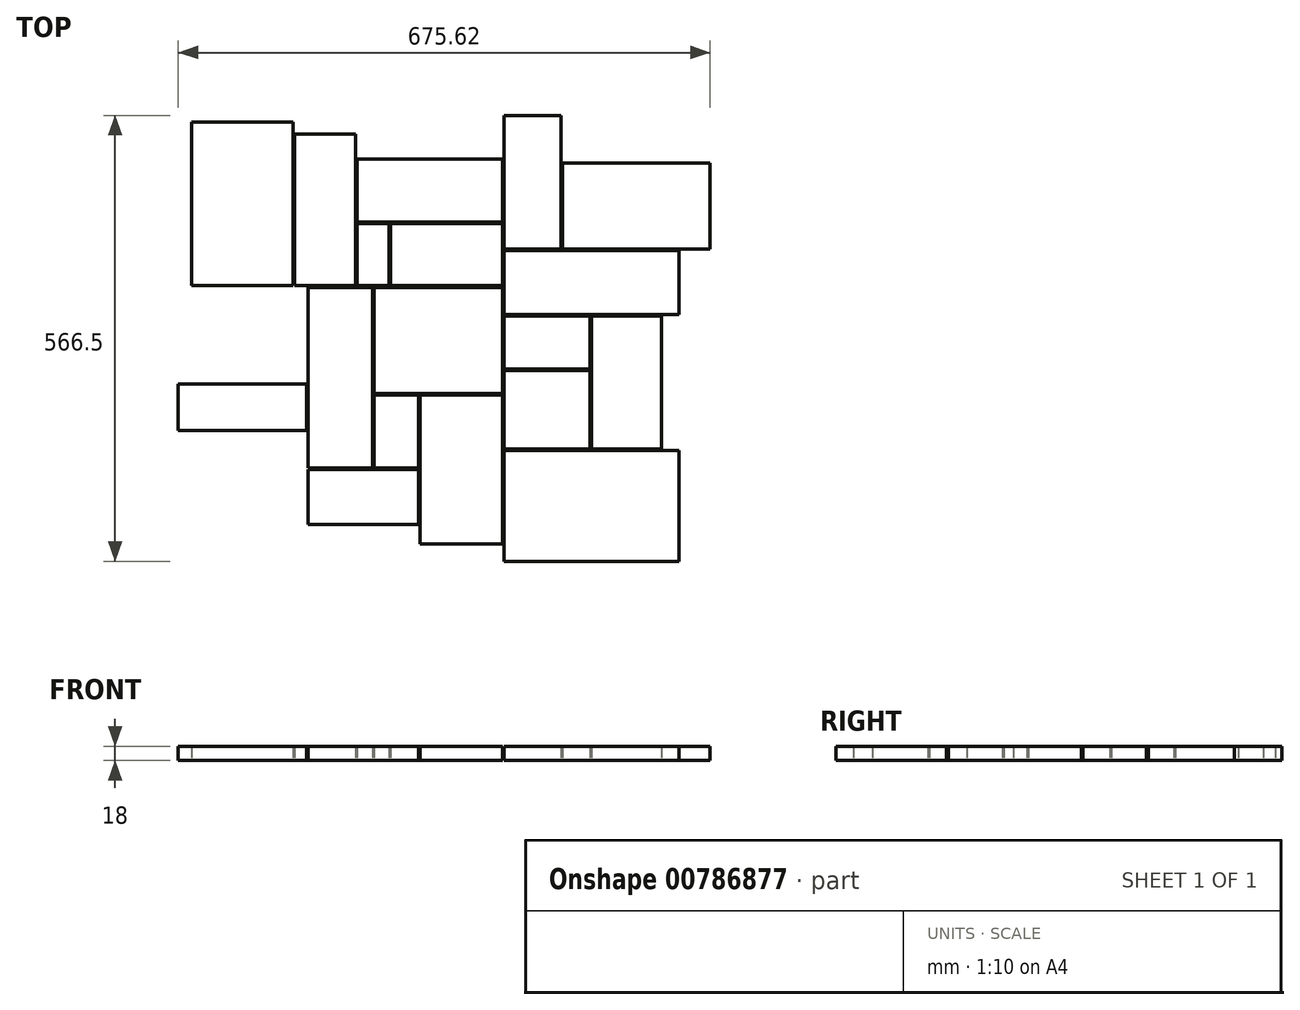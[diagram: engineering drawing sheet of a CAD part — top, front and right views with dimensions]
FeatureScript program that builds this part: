
annotation { "Feature Type Name" : "Feature", "Feature Type Description" : "" }
export const myFeature = defineFeature(function(context is Context, id is Id, definition is map)
    precondition{}
    {
        {
            var Q0;
            Q0=qCreatedBy(makeId("Top.planeOp"),FACE);
            var sketch = newSketch(context, id + "F0", { "sketchPlane" : qUnion([Q0])});
            skLineSegment(sketch, "E0.top", {"start": v(-7.38, -279.05) * mm, "end": v(214.62, -279.05) * mm});
            skLineSegment(sketch, "E0.right", {"start": v(214.62, -138.55) * mm, "end": v(214.62, -279.05) * mm});
            skLineSegment(sketch, "E1.right", {"start": v(192.62, -136.55) * mm, "end": v(192.62, 32.45) * mm});
            skLineSegment(sketch, "E2.right", {"start": v(214.62, 34.45) * mm, "end": v(214.62, 115.45) * mm});
            skLineSegment(sketch, "E3.top", {"start": v(-7.38, 287.45) * mm, "end": v(64.62, 287.45) * mm});
            skLineSegment(sketch, "E4.top", {"start": v(66.62, 226.95) * mm, "end": v(254.12, 226.95) * mm});
            skLineSegment(sketch, "E4.right", {"start": v(254.12, 117.45) * mm, "end": v(254.12, 226.95) * mm});
            skLineSegment(sketch, "E5.top", {"start": v(-114.5, -257.22) * mm, "end": v(-9.5, -257.22) * mm});
            skLineSegment(sketch, "E6.top", {"start": v(-9.38, 232.02) * mm, "end": v(-194.5, 232.02) * mm});
            skLineSegment(sketch, "E7.top", {"start": v(-116.5, -232.48) * mm, "end": v(-256.5, -232.48) * mm});
            skLineSegment(sketch, "E8.top", {"start": v(-196.5, 264.02) * mm, "end": v(-273.5, 264.02) * mm, "construction": true});
            skLineSegment(sketch, "E9.top", {"start": v(-275.5, 279.02) * mm, "end": v(-404.5, 279.02) * mm});
            skLineSegment(sketch, "E9.right", {"start": v(-404.5, 71.02) * mm, "end": v(-404.5, 279.02) * mm});
            skLineSegment(sketch, "E10.right", {"start": v(-443.5, 69.02) * mm, "end": v(-443.5, -52.98) * mm});
            skLineSegment(sketch, "E11.0", {"start": v(-273.5, 71.02) * mm, "end": v(-273.5, 264.02) * mm});
            skLineSegment(sketch, "E12.0", {"start": v(-275.5, 71.02) * mm, "end": v(-275.5, 279.02) * mm});
            skLineSegment(sketch, "E13", {"start": v(-273.5, 264.02) * mm, "end": v(-196.5, 264.02) * mm});
            skLineSegment(sketch, "E14.0", {"start": v(-194.5, 71.02) * mm, "end": v(-194.5, 150.02) * mm});
            skLineSegment(sketch, "E15.0", {"start": v(-196.5, 71.02) * mm, "end": v(-196.5, 264.02) * mm});
            skLineSegment(sketch, "E16.0", {"start": v(-9.38, 152.02) * mm, "end": v(-194.5, 152.02) * mm});
            skLineSegment(sketch, "E17.0", {"start": v(-9.38, 150.02) * mm, "end": v(-151.5, 150.02) * mm});
            skLineSegment(sketch, "E18.0", {"start": v(-153.5, 150.02) * mm, "end": v(-153.5, 71.02) * mm});
            skLineSegment(sketch, "E19.0", {"start": v(-151.5, 150.02) * mm, "end": v(-151.5, 71.02) * mm});
            skLineSegment(sketch, "E20.0", {"start": v(-172.5, 69.02) * mm, "end": v(-9.38, 69.02) * mm});
            skLineSegment(sketch, "E21.0", {"start": v(-173.5, 71.02) * mm, "end": v(-153.5, 71.02) * mm});
            skLineSegment(sketch, "E22.0", {"start": v(-196.5, 71.02) * mm, "end": v(-273.5, 71.02) * mm});
            skLineSegment(sketch, "E23.0", {"start": v(-194.5, 71.02) * mm, "end": v(-153.5, 71.02) * mm});
            skLineSegment(sketch, "E24.0", {"start": v(-195.5, 69.02) * mm, "end": v(-174.5, 69.02) * mm});
            skLineSegment(sketch, "E25.0", {"start": v(-195.5, 69.02) * mm, "end": v(-256.5, 69.02) * mm});
            skLineSegment(sketch, "E26.0", {"start": v(-404.5, 69.02) * mm, "end": v(-275.5, 69.02) * mm});
            skLineSegment(sketch, "E27.0", {"start": v(-258.5, 69.02) * mm, "end": v(-443.5, 69.02) * mm});
            skLineSegment(sketch, "E28.0", {"start": v(-256.5, 69.02) * mm, "end": v(-256.5, -52.98) * mm});
            skLineSegment(sketch, "E29.0", {"start": v(-258.5, 69.02) * mm, "end": v(-258.5, -51.98) * mm});
            skLineSegment(sketch, "E30.0", {"start": v(-9.5, 150.02) * mm, "end": v(-9.5, 71.02) * mm});
            skLineSegment(sketch, "E31.0", {"start": v(-7.38, 117.45) * mm, "end": v(-7.38, 287.45) * mm});
            skLineSegment(sketch, "E32.0", {"start": v(64.62, 117.45) * mm, "end": v(64.62, 287.45) * mm});
            skLineSegment(sketch, "E33.0", {"start": v(66.62, 117.45) * mm, "end": v(66.62, 226.95) * mm});
            skLineSegment(sketch, "E34.0", {"start": v(-7.5, 115.45) * mm, "end": v(214.62, 115.45) * mm});
            skLineSegment(sketch, "E35.0", {"start": v(-7.38, 117.45) * mm, "end": v(64.62, 117.45) * mm});
            skLineSegment(sketch, "E36.0", {"start": v(65.62, 115.45) * mm, "end": v(214.62, 115.45) * mm});
            skLineSegment(sketch, "E37.0", {"start": v(66.62, 117.45) * mm, "end": v(254.12, 117.45) * mm});
            skLineSegment(sketch, "E38.0", {"start": v(-7.38, 32.45) * mm, "end": v(101.62, 32.45) * mm});
            skLineSegment(sketch, "E39.0", {"start": v(-7.38, 34.45) * mm, "end": v(214.62, 34.45) * mm});
            skLineSegment(sketch, "E40.0", {"start": v(-7.38, 34.45) * mm, "end": v(-7.38, 115.45) * mm});
            skLineSegment(sketch, "E41.0", {"start": v(-9.38, 33.45) * mm, "end": v(-9.38, 69.02) * mm});
            skLineSegment(sketch, "E42.0", {"start": v(-7.38, -34.55) * mm, "end": v(-7.38, 32.45) * mm});
            skLineSegment(sketch, "E43.0", {"start": v(-9.38, -35.55) * mm, "end": v(-9.38, 33.45) * mm});
            skLineSegment(sketch, "E44.0", {"start": v(-7.38, -136.55) * mm, "end": v(-7.38, -36.55) * mm});
            skLineSegment(sketch, "E45.0", {"start": v(101.62, -34.55) * mm, "end": v(-7.38, -34.55) * mm});
            skLineSegment(sketch, "E46.0", {"start": v(101.62, -36.55) * mm, "end": v(-7.38, -36.55) * mm});
            skLineSegment(sketch, "E47.0", {"start": v(103.62, -136.55) * mm, "end": v(103.62, 32.45) * mm});
            skLineSegment(sketch, "E48.0", {"start": v(101.62, -136.55) * mm, "end": v(101.62, -36.55) * mm});
            skLineSegment(sketch, "E49.0", {"start": v(-7.38, -138.55) * mm, "end": v(102.62, -138.55) * mm});
            skLineSegment(sketch, "E50.0", {"start": v(-7.38, -136.55) * mm, "end": v(101.62, -136.55) * mm});
            skLineSegment(sketch, "E51.0", {"start": v(103.62, -136.55) * mm, "end": v(192.62, -136.55) * mm});
            skLineSegment(sketch, "E52.0", {"start": v(102.62, -138.55) * mm, "end": v(192.62, -138.55) * mm});
            skLineSegment(sketch, "E53.0", {"start": v(-7.38, -138.55) * mm, "end": v(214.62, -138.55) * mm});
            skLineSegment(sketch, "E54.0", {"start": v(-172.5, -67.98) * mm, "end": v(-116.5, -67.98) * mm});
            skLineSegment(sketch, "E55.0", {"start": v(-172.5, -65.98) * mm, "end": v(-9.38, -65.98) * mm});
            skLineSegment(sketch, "E56.0", {"start": v(-174.5, 69.02) * mm, "end": v(-174.5, -66.98) * mm});
            skLineSegment(sketch, "E57.0", {"start": v(-172.5, 69.02) * mm, "end": v(-172.5, -65.98) * mm});
            skLineSegment(sketch, "E58.0", {"start": v(-174.5, -66.98) * mm, "end": v(-174.5, -160.48) * mm});
            skLineSegment(sketch, "E59.0", {"start": v(-172.5, -67.98) * mm, "end": v(-172.5, -160.48) * mm});
            skLineSegment(sketch, "E60.0", {"start": v(-173.5, -162.48) * mm, "end": v(-116.5, -162.48) * mm});
            skLineSegment(sketch, "E60.1", {"start": v(-173.5, -162.48) * mm, "end": v(-256.5, -162.48) * mm});
            skLineSegment(sketch, "E61.0", {"start": v(-174.5, -160.48) * mm, "end": v(-256.5, -160.48) * mm});
            skLineSegment(sketch, "E61.1", {"start": v(-172.5, -160.48) * mm, "end": v(-116.5, -160.48) * mm});
            skLineSegment(sketch, "E62.0", {"start": v(-7.38, -138.55) * mm, "end": v(-7.38, -279.05) * mm});
            skLineSegment(sketch, "E63.0", {"start": v(-9.5, -67.98) * mm, "end": v(-9.5, -257.22) * mm});
            skLineSegment(sketch, "E64.0", {"start": v(-114.5, -67.98) * mm, "end": v(-114.5, -257.22) * mm});
            skLineSegment(sketch, "E65.0", {"start": v(-116.5, -67.98) * mm, "end": v(-116.5, -160.48) * mm});
            skLineSegment(sketch, "E66.0", {"start": v(-256.5, 69.02) * mm, "end": v(-256.5, -160.48) * mm});
            skLineSegment(sketch, "E67.0", {"start": v(-256.5, -113.98) * mm, "end": v(-256.5, -160.48) * mm});
            skLineSegment(sketch, "E68.0", {"start": v(-258.5, -51.98) * mm, "end": v(-421.5, -51.98) * mm});
            skLineSegment(sketch, "E69.0", {"start": v(-258.5, -51.98) * mm, "end": v(-443.5, -51.98) * mm});
            skLineSegment(sketch, "E70.0", {"start": v(-258.5, -53.98) * mm, "end": v(-421.5, -53.98) * mm});
            skLineSegment(sketch, "E71.0", {"start": v(-258.5, -112.98) * mm, "end": v(-403.5, -112.98) * mm});
            skLineSegment(sketch, "E72.0", {"start": v(-258.5, -114.98) * mm, "end": v(-403.5, -114.98) * mm});
            skLineSegment(sketch, "E73.0", {"start": v(-258.5, -112.98) * mm, "end": v(-421.5, -112.98) * mm});
            skLineSegment(sketch, "E74.0", {"start": v(-275.5, 71.02) * mm, "end": v(-404.5, 71.02) * mm});
            skLineSegment(sketch, "E75.trimOffspring", {"start": v(-258.5, 69.02) * mm, "end": v(-274.5, 69.02) * mm});
            skLineSegment(sketch, "E76.trimOffspring", {"start": v(-172.5, 69.02) * mm, "end": v(-152.5, 69.02) * mm});
            skLineSegment(sketch, "E77.trimOffspring", {"start": v(-151.5, 71.02) * mm, "end": v(-9.38, 71.02) * mm});
            skLineSegment(sketch, "E78.trimOffspring", {"start": v(-194.5, 152.02) * mm, "end": v(-194.5, 232.02) * mm});
            skLineSegment(sketch, "E79.trimOffspring", {"start": v(-153.5, 150.02) * mm, "end": v(-194.5, 150.02) * mm});
            skLineSegment(sketch, "E80.trimOffspring", {"start": v(-9.38, 152.02) * mm, "end": v(-9.38, 232.02) * mm});
            skLineSegment(sketch, "E81.trimOffspring", {"start": v(66.62, 117.45) * mm, "end": v(214.62, 117.45) * mm});
            skLineSegment(sketch, "E82.trimOffspring", {"start": v(103.62, 32.45) * mm, "end": v(192.62, 32.45) * mm});
            skLineSegment(sketch, "E83", {"start": v(-421.5, -53.98) * mm, "end": v(-421.5, -112.98) * mm});
            skLineSegment(sketch, "E84", {"start": v(-403.5, -114.98) * mm, "end": v(-403.5, -258.26) * mm});
            skLineSegment(sketch, "E85.trimOffspring", {"start": v(-258.5, -53.98) * mm, "end": v(-258.5, -112.98) * mm});
            skLineSegment(sketch, "E86.trimOffspring", {"start": v(-256.5, -162.48) * mm, "end": v(-256.5, -232.48) * mm});
            skLineSegment(sketch, "E87.trimOffspring", {"start": v(-114.5, -67.98) * mm, "end": v(-9.38, -67.98) * mm});
            skLineSegment(sketch, "E88.trimOffspring", {"start": v(-9.38, -65.98) * mm, "end": v(-9.38, -35.55) * mm});
            skLineSegment(sketch, "E89.trimOffspring", {"start": v(101.62, -34.55) * mm, "end": v(101.62, 32.45) * mm});
            skLineSegment(sketch, "E90.trimOffspring", {"start": v(-116.5, -162.48) * mm, "end": v(-116.5, -232.48) * mm});
            skLineSegment(sketch, "E91.top", {"start": v(-258.5, -258.26) * mm, "end": v(-403.5, -258.26) * mm});
            skLineSegment(sketch, "E91.left", {"start": v(-258.5, -114.98) * mm, "end": v(-258.5, -258.26) * mm});
            skSolve(sketch);
        }
        {
            var Q0;
            Q0=makeQuery(id+"F0.imprint","IMPRINT",FACE,{"disambiguationData":[TD([[makeQuery(id+"F0.imprint","IMPRINT",EDGE,{"derivedFrom":sQuery(id+"F0.wireOp",EDGE,"E72.0")}),1.0]])]});
            var Q1;
            Q1=makeQuery(id+"F0.imprint","IMPRINT",FACE,{"disambiguationData":[TD([[makeQuery(id+"F0.imprint","IMPRINT",EDGE,{"derivedFrom":sQuery(id+"F0.wireOp",EDGE,"E38.0")}),-1.0]])]});
            var Q2;
            Q2=makeQuery(id+"F0.imprint","IMPRINT",FACE,{"disambiguationData":[TD([[makeQuery(id+"F0.imprint","IMPRINT",EDGE,{"derivedFrom":sQuery(id+"F0.wireOp",EDGE,"E20.0")}),-1.0]])]});
            var Q3;
            Q3=makeQuery(id+"F0.imprint","IMPRINT",FACE,{"disambiguationData":[TD([[makeQuery(id+"F0.imprint","IMPRINT",EDGE,{"derivedFrom":sQuery(id+"F0.wireOp",EDGE,"E44.0")}),-1.0]])]});
            var Q4;
            Q4=makeQuery(id+"F0.imprint","IMPRINT",FACE,{"disambiguationData":[TD([[makeQuery(id+"F0.imprint","IMPRINT",EDGE,{"derivedFrom":sQuery(id+"F0.wireOp",EDGE,"E24.0")}),-1.0]])]});
            var Q5;
            Q5=makeQuery(id+"F0.imprint","IMPRINT",FACE,{"disambiguationData":[TD([[makeQuery(id+"F0.imprint","IMPRINT",EDGE,{"derivedFrom":sQuery(id+"F0.wireOp",EDGE,"E0.top")}),1.0]])]});
            var Q6;
            Q6=makeQuery(id+"F0.imprint","IMPRINT",FACE,{"disambiguationData":[TD([[makeQuery(id+"F0.imprint","IMPRINT",EDGE,{"derivedFrom":sQuery(id+"F0.wireOp",EDGE,"E1.right")}),1.0]])]});
            var Q7;
            Q7=makeQuery(id+"F0.imprint","IMPRINT",FACE,{"disambiguationData":[TD([[makeQuery(id+"F0.imprint","IMPRINT",EDGE,{"derivedFrom":sQuery(id+"F0.wireOp",EDGE,"E2.right")}),1.0]])]});
            var Q8;
            Q8=makeQuery(id+"F0.imprint","IMPRINT",FACE,{"disambiguationData":[TD([[makeQuery(id+"F0.imprint","IMPRINT",EDGE,{"derivedFrom":sQuery(id+"F0.wireOp",EDGE,"E3.top")}),-1.0]])]});
            var Q9;
            Q9=makeQuery(id+"F0.imprint","IMPRINT",FACE,{"disambiguationData":[TD([[makeQuery(id+"F0.imprint","IMPRINT",EDGE,{"derivedFrom":sQuery(id+"F0.wireOp",EDGE,"E4.top")}),-1.0]])]});
            var Q10;
            Q10=makeQuery(id+"F0.imprint","IMPRINT",FACE,{"disambiguationData":[TD([[makeQuery(id+"F0.imprint","IMPRINT",EDGE,{"derivedFrom":sQuery(id+"F0.wireOp",EDGE,"E5.top")}),1.0]])]});
            var Q11;
            Q11=makeQuery(id+"F0.imprint","IMPRINT",FACE,{"disambiguationData":[TD([[makeQuery(id+"F0.imprint","IMPRINT",EDGE,{"derivedFrom":sQuery(id+"F0.wireOp",EDGE,"E6.top")}),1.0]])]});
            var Q12;
            {var subQ9=sQuery(id+"F0.wireOp",EDGE,"E29.0");Q12=makeQuery(id+"F0.imprint","IMPRINT",FACE,{"disambiguationData":[TD([[makeQuery(id+"F0.imprint","IMPRINT",EDGE,{"derivedFrom":subQ9}),-1.0]])]});}
            var Q13;
            Q13=makeQuery(id+"F0.imprint","IMPRINT",FACE,{"disambiguationData":[TD([[makeQuery(id+"F0.imprint","IMPRINT",EDGE,{"derivedFrom":sQuery(id+"F0.wireOp",EDGE,"E7.top")}),-1.0]])]});
            var Q14;
            Q14=makeQuery(id+"F0.imprint","IMPRINT",FACE,{"disambiguationData":[TD([[makeQuery(id+"F0.imprint","IMPRINT",EDGE,{"derivedFrom":sQuery(id+"F0.wireOp",EDGE,"E11.0")}),-1.0]])]});
            var Q15;
            Q15=makeQuery(id+"F0.imprint","IMPRINT",FACE,{"disambiguationData":[TD([[makeQuery(id+"F0.imprint","IMPRINT",EDGE,{"derivedFrom":sQuery(id+"F0.wireOp",EDGE,"E9.top")}),1.0]])]});
            var Q16;
            {var subQ1=sQuery(id+"F0.wireOp",EDGE,"E14.0");Q16=makeQuery(id+"F0.imprint","IMPRINT",FACE,{"disambiguationData":[TD([[makeQuery(id+"F0.imprint","IMPRINT",EDGE,{"derivedFrom":subQ1}),-1.0]])]});}
            var Q17;
            {var subQ0=sQuery(id+"F0.wireOp",EDGE,"E19.0");Q17=makeQuery(id+"F0.imprint","IMPRINT",FACE,{"disambiguationData":[TD([[makeQuery(id+"F0.imprint","IMPRINT",EDGE,{"derivedFrom":subQ0}),1.0]])]});}
            var Q18;
            Q18=makeQuery(id+"F0.imprint","IMPRINT",FACE,{"disambiguationData":[TD([[makeQuery(id+"F0.imprint","IMPRINT",EDGE,{"derivedFrom":sQuery(id+"F0.wireOp",EDGE,"E54.0")}),-1.0]])]});
            var Q19;
            Q19=makeQuery(id+"F0.imprint","IMPRINT",FACE,{"disambiguationData":[TD([[makeQuery(id+"F0.imprint","IMPRINT",EDGE,{"derivedFrom":sQuery(id+"F0.wireOp",EDGE,"E70.0")}),1.0]])]});
            extrude(context, id + "F1", {"entities" : qUnion([Q0, Q1, Q2, Q3, Q4, Q5, Q6, Q7, Q8, Q9, Q10, Q11, Q12, Q13, Q14, Q15, Q16, Q17, Q18, Q19]), "depth" : 18 * mm, "offsetDistance" : 25 * mm});
        }
    });
